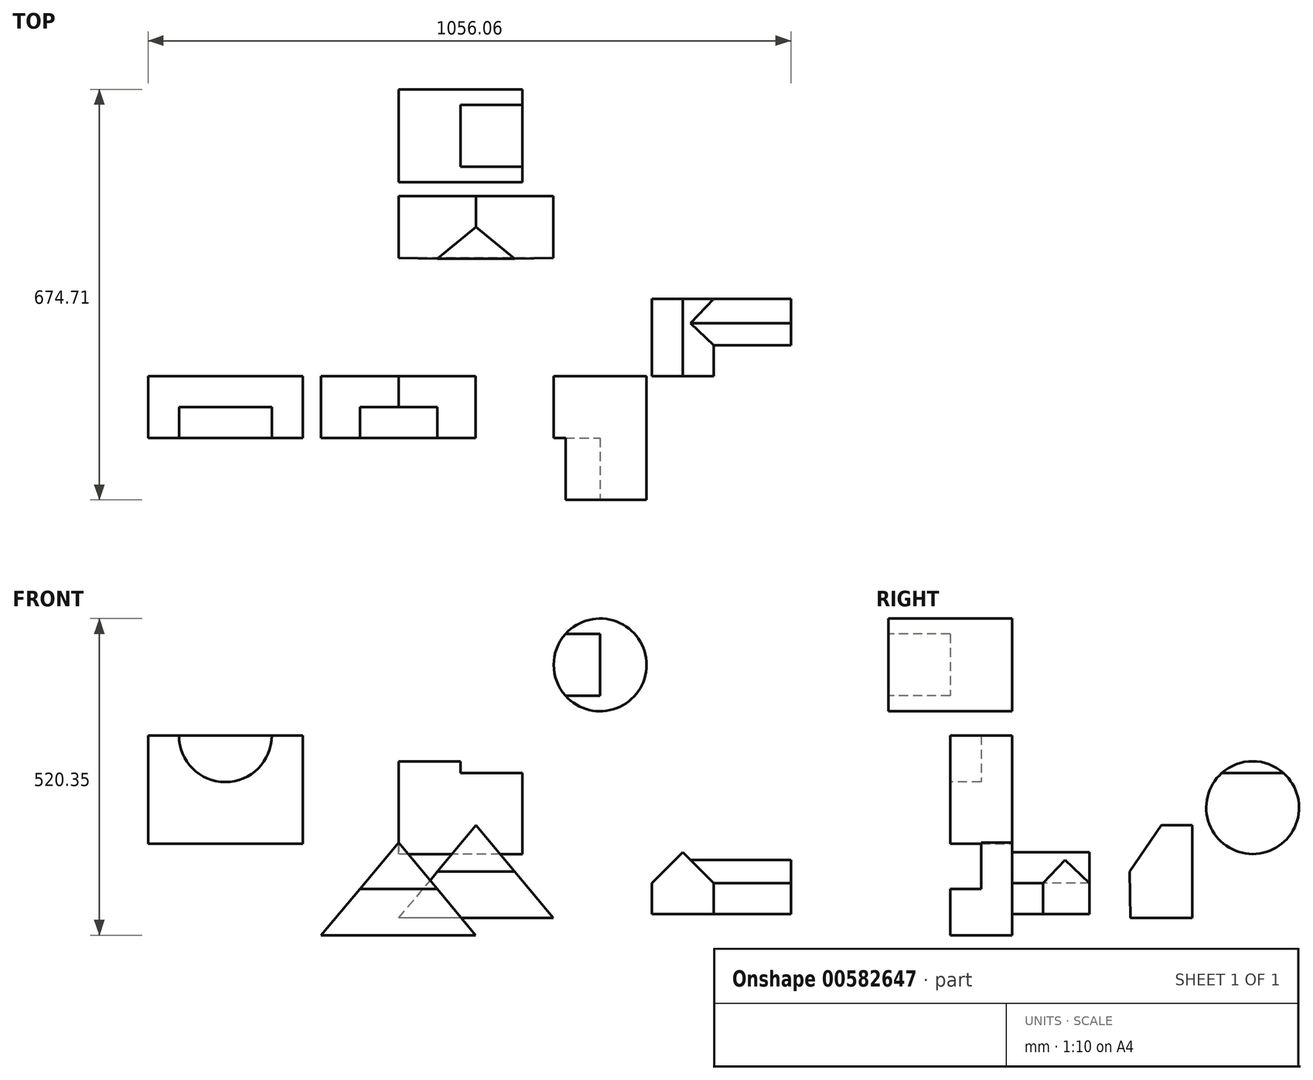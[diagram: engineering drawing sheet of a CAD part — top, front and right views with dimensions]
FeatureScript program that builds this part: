
annotation { "Feature Type Name" : "Feature", "Feature Type Description" : "" }
export const myFeature = defineFeature(function(context is Context, id is Id, definition is map)
    precondition{}
    {
        {
            var Q0;
            Q0=qCreatedBy(makeId("Front.planeOp"),FACE);
            var sketch = newSketch(context, id + "F0", { "sketchPlane" : qUnion([Q0])});
            skLineSegment(sketch, "E0", {"start": v(-127.64, -152.4) * mm, "end": v(126.36, -152.4) * mm});
            skLineSegment(sketch, "E1", {"start": v(126.36, -152.4) * mm, "end": v(0, 0) * mm});
            skLineSegment(sketch, "E2", {"start": v(0, 0) * mm, "end": v(-127.64, -152.4) * mm});
            skSolve(sketch);
        }
        {
            var Q0;
            Q0=makeQuery(id+"F0.imprint","IMPRINT",FACE,{"disambiguationData":[TD([[makeQuery(id+"F0.imprint","IMPRINT",EDGE,{"derivedFrom":sQuery(id+"F0.wireOp",EDGE,"E0")}),1.0]])]});
            extrude(context, id + "F1", {"entities" : qUnion([Q0]), "depth" : 101.6 * mm, "offsetDistance" : 25.4 * mm});
        }
        {
            var Q0;
            Q0=makeQuery(id+"F1.opExtrude","CAP_FACE",FACE,{"disambiguationData":[OSD([sQuery(id+"F0.wireOp",EDGE,"E0"),sQuery(id+"F0.wireOp",EDGE,"E1"),sQuery(id+"F0.wireOp",EDGE,"E2")])],"isStart":false});
            var sketch = newSketch(context, id + "F2", { "sketchPlane" : qUnion([Q0])});
            skPoint(sketch, "E3.firstSnap0", {"position": v(-63.82, -76.2) * mm});
            skLineSegment(sketch, "E3.bottom", {"start": v(-118.55, -76.2) * mm, "end": v(148.53, -76.2) * mm});
            skLineSegment(sketch, "E3.top", {"start": v(-118.55, 33.34) * mm, "end": v(148.53, 33.34) * mm});
            skLineSegment(sketch, "E3.left", {"start": v(-118.55, -76.2) * mm, "end": v(-118.55, 33.34) * mm});
            skLineSegment(sketch, "E3.right", {"start": v(148.53, -76.2) * mm, "end": v(148.53, 33.34) * mm});
            skSolve(sketch);
        }
        {
            var Q0;
            {var subQ0=sQuery(id+"F2.wireOp",EDGE,"E3.bottom");var subQ1=makeQuery(id+"F1.opExtrude","CAP_EDGE",EDGE,{"disambiguationData":[OSD([sQuery(id+"F0.wireOp",EDGE,"E2")])],"isStart":false});var subQ2=makeQuery(id+"F2.imprint","INTERSECT",VERTEX,{"derivedFrom":[subQ1,subQ0]});Q0=makeQuery(id+"F2.imprint","IMPRINT",FACE,{"disambiguationData":[TD([[makeQuery(id+"F2.imprint","IMPRINT",EDGE,{"disambiguationData":[TD([[subQ2,-1.0]])],"derivedFrom":subQ0}),1.0]])]});}
            extrude(context, id + "F3", {"entities" : qUnion([Q0]), "operationType" : NewBodyOperationType.REMOVE, "oppositeDirection" : true, "depth" : 50.8 * mm, "offsetDistance" : 25.4 * mm});
        }
        {
            var Q0;
            Q0=qCreatedBy(makeId("Right.planeOp"),FACE);
            var sketch = newSketch(context, id + "F4", { "sketchPlane" : qUnion([Q0])});
            skLineSegment(sketch, "E4", {"start": v(194.32, -124.23) * mm, "end": v(295.92, -124.23) * mm});
            skLineSegment(sketch, "E5", {"start": v(295.92, -124.23) * mm, "end": v(295.92, 28.17) * mm});
            skLineSegment(sketch, "E6", {"start": v(295.92, 28.17) * mm, "end": v(245.12, 28.17) * mm});
            skLineSegment(sketch, "E7", {"start": v(245.12, 28.17) * mm, "end": v(193.36, -48.04) * mm});
            skLineSegment(sketch, "E8", {"start": v(193.36, -48.04) * mm, "end": v(194.32, -124.23) * mm});
            skSolve(sketch);
        }
        {
            var Q0;
            Q0=makeQuery(id+"F4.imprint","IMPRINT",FACE,{"disambiguationData":[TD([[makeQuery(id+"F4.imprint","IMPRINT",EDGE,{"derivedFrom":sQuery(id+"F4.wireOp",EDGE,"E4")}),1.0]])]});
            extrude(context, id + "F5", {"entities" : qUnion([Q0]), "depth" : 254 * mm, "offsetDistance" : 25.4 * mm});
        }
        {
            var Q0;
            Q0=makeQuery(id+"F5.opExtrude","SWEPT_FACE",FACE,{"disambiguationData":[OSD([sQuery(id+"F4.wireOp",EDGE,"E5")])]});
            var sketch = newSketch(context, id + "F6", { "sketchPlane" : qUnion([Q0])});
            skLineSegment(sketch, "E9", {"start": v(-254, -124.23) * mm, "end": v(-127, 28.17) * mm});
            skLineSegment(sketch, "E10", {"start": v(-127, 28.17) * mm, "end": v(0, -124.23) * mm});
            skLineSegment(sketch, "E11", {"start": v(0, -124.23) * mm, "end": v(0, 28.17) * mm});
            skLineSegment(sketch, "E12", {"start": v(0, 28.17) * mm, "end": v(-254, 28.17) * mm});
            skLineSegment(sketch, "E13", {"start": v(-254, 28.17) * mm, "end": v(-254, -124.23) * mm});
            skSolve(sketch);
        }
        {
            var Q0;
            {var subQ0=sQuery(id+"F6.wireOp",EDGE,"E9");Q0=makeQuery(id+"F6.imprint","IMPRINT",FACE,{"disambiguationData":[TD([[makeQuery(id+"F6.imprint","IMPRINT",EDGE,{"derivedFrom":subQ0}),1.0]])]});}
            extrude(context, id + "F7", {"entities" : qUnion([Q0]), "operationType" : NewBodyOperationType.REMOVE, "oppositeDirection" : true, "depth" : 254 * mm, "offsetDistance" : 25.4 * mm});
        }
        {
            var Q0;
            Q0=makeQuery(id+"F5.opExtrude","SWEPT_FACE",FACE,{"disambiguationData":[OSD([sQuery(id+"F4.wireOp",EDGE,"E5")])]});
            var sketch = newSketch(context, id + "F8", { "sketchPlane" : qUnion([Q0])});
            skLineSegment(sketch, "E14", {"start": v(0, -124.23) * mm, "end": v(-127, 28.17) * mm});
            skLineSegment(sketch, "E15", {"start": v(-127, 28.17) * mm, "end": v(0, 28.17) * mm});
            skLineSegment(sketch, "E16", {"start": v(0, 28.17) * mm, "end": v(0, -124.23) * mm});
            skSolve(sketch);
        }
        {
            var Q0;
            Q0=makeQuery(id+"F8.imprint","IMPRINT",FACE,{"disambiguationData":[TD([[makeQuery(id+"F8.imprint","IMPRINT",EDGE,{"derivedFrom":sQuery(id+"F8.wireOp",EDGE,"E14")}),-1.0]])]});
            extrude(context, id + "F9", {"entities" : qUnion([Q0]), "operationType" : NewBodyOperationType.REMOVE, "oppositeDirection" : true, "depth" : 254 * mm, "offsetDistance" : 25.4 * mm});
        }
        {
            var Q0;
            Q0=qCreatedBy(makeId("Front.planeOp"),FACE);
            var sketch = newSketch(context, id + "F10", { "sketchPlane" : qUnion([Q0])});
            skLineSegment(sketch, "E17", {"start": v(415.6, -117.7) * mm, "end": v(517.2, -117.7) * mm});
            skLineSegment(sketch, "E18", {"start": v(517.2, -117.7) * mm, "end": v(517.2, -66.9) * mm});
            skLineSegment(sketch, "E19", {"start": v(517.2, -66.9) * mm, "end": v(466.4, -16.1) * mm});
            skPoint(sketch, "E19.endSnap0", {"position": v(466.4, -117.7) * mm});
            skLineSegment(sketch, "E20", {"start": v(466.4, -16.1) * mm, "end": v(415.6, -66.9) * mm});
            skLineSegment(sketch, "E21", {"start": v(415.6, -66.9) * mm, "end": v(415.6, -117.7) * mm});
            skSolve(sketch);
        }
        {
            var Q0;
            Q0 = qSketchRegion(id + "F10", true);
            extrude(context, id + "F11", {"entities" : qUnion([Q0]), "oppositeDirection" : true, "depth" : 127 * mm, "offsetDistance" : 25.4 * mm});
        }
        {
            var Q0;
            Q0=makeQuery(id+"F11.opExtrude","SWEPT_FACE",FACE,{"disambiguationData":[OSD([sQuery(id+"F10.wireOp",EDGE,"E18")])]});
            var sketch = newSketch(context, id + "F12", { "sketchPlane" : qUnion([Q0])});
            skLineSegment(sketch, "E22", {"start": v(127, -117.7) * mm, "end": v(50.8, -117.7) * mm});
            skLineSegment(sketch, "E23", {"start": v(50.8, -117.7) * mm, "end": v(50.8, -66.9) * mm});
            skLineSegment(sketch, "E24", {"start": v(50.8, -66.9) * mm, "end": v(87, -28.8) * mm});
            skLineSegment(sketch, "E25", {"start": v(87, -28.8) * mm, "end": v(127, -66.9) * mm});
            skLineSegment(sketch, "E26", {"start": v(127, -66.9) * mm, "end": v(127, -117.7) * mm});
            skSolve(sketch);
        }
        {
            var Q0;
            Q0=makeQuery(id+"F12.imprint","IMPRINT",FACE,{"disambiguationData":[TD([[makeQuery(id+"F12.imprint","IMPRINT",EDGE,{"derivedFrom":sQuery(id+"F12.wireOp",EDGE,"E22")}),-1.0]])]});
            var Q1;
            {var subQ0=sQuery(id+"F12.wireOp",EDGE,"E24");Q1=makeQuery(id+"F12.imprint","IMPRINT",FACE,{"disambiguationData":[TD([[makeQuery(id+"F12.imprint","IMPRINT",EDGE,{"derivedFrom":subQ0}),-1.0]])]});}
            extrude(context, id + "F13", {"entities" : qUnion([Q0, Q1]), "operationType" : NewBodyOperationType.ADD, "depth" : 127 * mm, "offsetDistance" : 25.4 * mm});
        }
        {
            var Q0;
            {var subQ0=sQuery(id+"F12.wireOp",EDGE,"E24");Q0=makeQuery(id+"F12.imprint","IMPRINT",FACE,{"disambiguationData":[TD([[makeQuery(id+"F12.imprint","IMPRINT",EDGE,{"derivedFrom":subQ0}),-1.0]])]});}
            extrude(context, id + "F14", {"entities" : qUnion([Q0]), "operationType" : NewBodyOperationType.ADD, "endBound" : BoundingType.UP_TO_NEXT, "oppositeDirection" : true, "depth" : 25.4 * mm, "offsetDistance" : 25.4 * mm});
        }
        {
            var Q0;
            Q0=qCreatedBy(makeId("Right.planeOp"),FACE);
            var sketch = newSketch(context, id + "F15", { "sketchPlane" : qUnion([Q0])});
            skCircle(sketch, "E27", {"center": v(395.31, 57.15) * mm, "radius": 76.2 * mm});
            skSolve(sketch);
        }
        {
            var Q0;
            Q0=makeQuery(id+"F15.imprint","IMPRINT",FACE,{"disambiguationData":[TD([[makeQuery(id+"F15.imprint","IMPRINT",EDGE,{"derivedFrom":sQuery(id+"F15.wireOp",EDGE,"E27")}),1.0]])]});
            extrude(context, id + "F16", {"entities" : qUnion([Q0]), "depth" : 203.2 * mm, "offsetDistance" : 25.4 * mm});
        }
        {
            var Q0;
            Q0=makeQuery(id+"F16.opExtrude","CAP_FACE",FACE,{"disambiguationData":[OSD([sQuery(id+"F15.wireOp",EDGE,"E27")])],"isStart":false});
            var sketch = newSketch(context, id + "F17", { "sketchPlane" : qUnion([Q0])});
            skLineSegment(sketch, "E28", {"start": v(344.51, 113.95) * mm, "end": v(446.11, 113.95) * mm});
            skSolve(sketch);
        }
        {
            var Q0;
            {var subQ0=sQuery(id+"F17.wireOp",EDGE,"E28");Q0=makeQuery(id+"F17.imprint","IMPRINT",FACE,{"disambiguationData":[TD([[makeQuery(id+"F17.imprint","IMPRINT",EDGE,{"derivedFrom":subQ0}),1.0]])]});}
            extrude(context, id + "F18", {"entities" : qUnion([Q0]), "operationType" : NewBodyOperationType.REMOVE, "oppositeDirection" : true, "depth" : 101.6 * mm, "offsetDistance" : 25.4 * mm});
        }
        {
            var Q0;
            Q0=qCreatedBy(makeId("Front.planeOp"),FACE);
            var sketch = newSketch(context, id + "F19", { "sketchPlane" : qUnion([Q0])});
            skCircle(sketch, "E29", {"center": v(330.74, 291.75) * mm, "radius": 76.2 * mm});
            skSolve(sketch);
        }
        {
            var Q0;
            Q0 = qSketchRegion(id + "F19", true);
            extrude(context, id + "F20", {"entities" : qUnion([Q0]), "depth" : 203.2 * mm, "offsetDistance" : 25.4 * mm});
        }
        {
            var Q0;
            Q0=makeQuery(id+"F20.opExtrude","CAP_FACE",FACE,{"disambiguationData":[OSD([sQuery(id+"F19.wireOp",EDGE,"E29")])],"isStart":false});
            var sketch = newSketch(context, id + "F21", { "sketchPlane" : qUnion([Q0])});
            skLineSegment(sketch, "E30", {"start": v(273.94, 342.55) * mm, "end": v(330.74, 342.55) * mm});
            skLineSegment(sketch, "E31", {"start": v(330.74, 342.55) * mm, "end": v(330.74, 240.95) * mm});
            skLineSegment(sketch, "E32", {"start": v(330.74, 240.95) * mm, "end": v(273.94, 240.95) * mm});
            skSolve(sketch);
        }
        {
            var Q0;
            Q0 = qSketchRegion(id + "F21", true);
            var Q1;
            {var subQ0=sQuery(id+"F21.wireOp",EDGE,"E30");Q1=makeQuery(id+"F21.imprint","IMPRINT",FACE,{"disambiguationData":[TD([[makeQuery(id+"F21.imprint","IMPRINT",EDGE,{"derivedFrom":subQ0}),-1.0]])]});}
            extrude(context, id + "F22", {"entities" : qUnion([Q0, Q1]), "operationType" : NewBodyOperationType.REMOVE, "oppositeDirection" : true, "depth" : 101.6 * mm, "offsetDistance" : 25.4 * mm});
        }
        {
            var Q0;
            Q0=qCreatedBy(makeId("Front.planeOp"),FACE);
            var sketch = newSketch(context, id + "F23", { "sketchPlane" : qUnion([Q0])});
            skLineSegment(sketch, "E33", {"start": v(-411.85, -2.34) * mm, "end": v(-157.85, -2.34) * mm});
            skLineSegment(sketch, "E34", {"start": v(-157.85, -2.34) * mm, "end": v(-157.85, 175.46) * mm});
            skLineSegment(sketch, "E35", {"start": v(-157.85, 175.46) * mm, "end": v(-411.85, 175.46) * mm});
            skLineSegment(sketch, "E36", {"start": v(-411.85, 175.46) * mm, "end": v(-411.85, -2.34) * mm});
            skSolve(sketch);
        }
        {
            var Q0;
            Q0 = qSketchRegion(id + "F23", true);
            extrude(context, id + "F24", {"entities" : qUnion([Q0]), "depth" : 101.6 * mm, "offsetDistance" : 25.4 * mm});
        }
        {
            var Q0;
            Q0=makeQuery(id+"F24.opExtrude","CAP_FACE",FACE,{"disambiguationData":[OSD([sQuery(id+"F23.wireOp",EDGE,"E33"),sQuery(id+"F23.wireOp",EDGE,"E34"),sQuery(id+"F23.wireOp",EDGE,"E35"),sQuery(id+"F23.wireOp",EDGE,"E36")])],"isStart":false});
            var sketch = newSketch(context, id + "F25", { "sketchPlane" : qUnion([Q0])});
            skCircle(sketch, "E37", {"center": v(-284.85, 175.46) * mm, "radius": 76.2 * mm});
            skSolve(sketch);
        }
        {
            var Q0;
            {var subQ0=sQuery(id+"F25.wireOp",EDGE,"E37");var subQ1=makeQuery(id+"F24.opExtrude","CAP_EDGE",EDGE,{"disambiguationData":[OSD([sQuery(id+"F23.wireOp",EDGE,"E35")])],"isStart":false});var subQ2=makeQuery(id+"F25.imprint","INTERSECT",VERTEX,{"disambiguationData":[OD(0.0)],"derivedFrom":[subQ1,subQ0]});Q0=makeQuery(id+"F25.imprint","IMPRINT",FACE,{"disambiguationData":[TD([[makeQuery(id+"F25.imprint","IMPRINT",EDGE,{"disambiguationData":[TD([[subQ2,-1.0]])],"derivedFrom":subQ0}),1.0]])]});}
            var Q1;
            {var subQ0=sQuery(id+"F25.wireOp",EDGE,"E37");var subQ1=makeQuery(id+"F24.opExtrude","CAP_EDGE",EDGE,{"disambiguationData":[OSD([sQuery(id+"F23.wireOp",EDGE,"E35")])],"isStart":false});var subQ2=makeQuery(id+"F25.imprint","INTERSECT",VERTEX,{"disambiguationData":[OD(0.0)],"derivedFrom":[subQ1,subQ0]});Q1=makeQuery(id+"F25.imprint","IMPRINT",FACE,{"disambiguationData":[TD([[makeQuery(id+"F25.imprint","IMPRINT",EDGE,{"disambiguationData":[TD([[subQ2,1.0]])],"derivedFrom":subQ0}),1.0]])]});}
            extrude(context, id + "F26", {"entities" : qUnion([Q0, Q1]), "operationType" : NewBodyOperationType.REMOVE, "oppositeDirection" : true, "depth" : 50.8 * mm, "offsetDistance" : 25.4 * mm});
        }
    });
